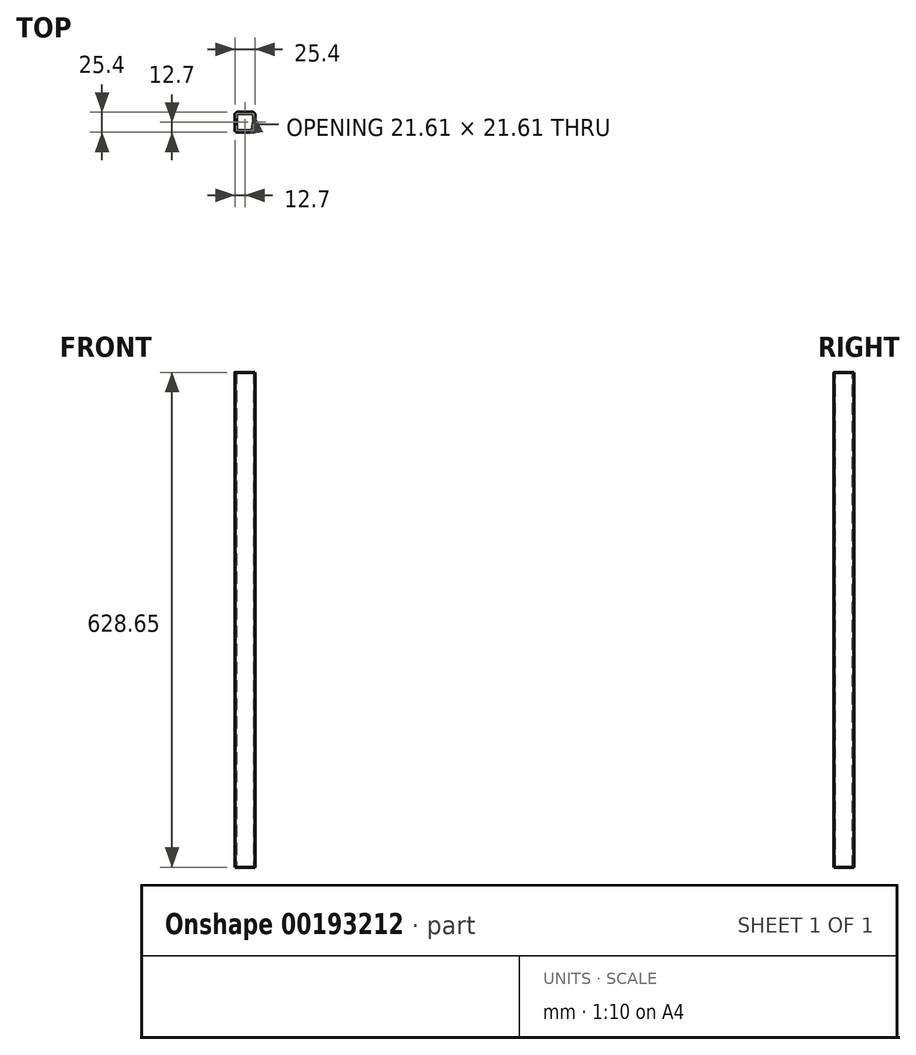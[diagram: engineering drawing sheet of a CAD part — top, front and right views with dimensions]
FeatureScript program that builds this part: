
annotation { "Feature Type Name" : "Feature", "Feature Type Description" : "" }
export const myFeature = defineFeature(function(context is Context, id is Id, definition is map)
    precondition{}
    {
        {
            var Q0;
            Q0=qCreatedBy(makeId("Top.planeOp"),FACE);
            var sketch = newSketch(context, id + "F0", { "sketchPlane" : qUnion([Q0])});
            skLineSegment(sketch, "E0.bottom", {"start": v(3.18, 0) * mm, "end": v(22.23, 0) * mm});
            skLineSegment(sketch, "E0.top", {"start": v(3.18, -25.4) * mm, "end": v(22.23, -25.4) * mm});
            skLineSegment(sketch, "E0.left", {"start": v(0, -3.18) * mm, "end": v(0, -22.23) * mm});
            skLineSegment(sketch, "E0.right", {"start": v(25.4, -3.18) * mm, "end": v(25.4, -22.23) * mm});
            skPoint(sketch, "E1.visualSharp", {"position": v(0, 0) * mm});
            skArc(sketch, "E1.filletArc", {"start": v(3.18, 0) * mm, "mid": v(0.93, -0.93) * mm, "end": v(0, -3.18) * mm});
            skPoint(sketch, "E2.visualSharp", {"position": v(25.4, 0) * mm});
            skArc(sketch, "E2.filletArc", {"start": v(25.4, -3.18) * mm, "mid": v(24.47, -0.93) * mm, "end": v(22.23, 0) * mm});
            skPoint(sketch, "E3.visualSharp", {"position": v(25.4, -25.4) * mm});
            skArc(sketch, "E3.filletArc", {"start": v(22.23, -25.4) * mm, "mid": v(24.47, -24.47) * mm, "end": v(25.4, -22.23) * mm});
            skPoint(sketch, "E4.visualSharp", {"position": v(0, -25.4) * mm});
            skArc(sketch, "E4.filletArc", {"start": v(0, -22.23) * mm, "mid": v(0.93, -24.47) * mm, "end": v(3.18, -25.4) * mm});
            skSolve(sketch);
        }
        {
            var Q0;
            Q0 = qSketchRegion(id + "F0", true);
            extrude(context, id + "F1", {"entities" : qUnion([Q0]), "depth" : 628.65 * mm});
        }
        {
            var Q0;
            Q0=makeQuery(id+"F1.opExtrude","CAP_FACE",FACE,{"disambiguationData":[OSD([sQuery(id+"F0.wireOp",EDGE,"E0.bottom"),sQuery(id+"F0.wireOp",EDGE,"E0.top"),sQuery(id+"F0.wireOp",EDGE,"E0.left"),sQuery(id+"F0.wireOp",EDGE,"E0.right"),sQuery(id+"F0.wireOp",EDGE,"E1.filletArc"),sQuery(id+"F0.wireOp",EDGE,"E2.filletArc"),sQuery(id+"F0.wireOp",EDGE,"E3.filletArc"),sQuery(id+"F0.wireOp",EDGE,"E4.filletArc")])],"isStart":false});
            var Q1;
            Q1=makeQuery(id+"F1.opExtrude","CAP_FACE",FACE,{"disambiguationData":[OSD([sQuery(id+"F0.wireOp",EDGE,"E0.bottom"),sQuery(id+"F0.wireOp",EDGE,"E0.top"),sQuery(id+"F0.wireOp",EDGE,"E0.left"),sQuery(id+"F0.wireOp",EDGE,"E0.right"),sQuery(id+"F0.wireOp",EDGE,"E1.filletArc"),sQuery(id+"F0.wireOp",EDGE,"E2.filletArc"),sQuery(id+"F0.wireOp",EDGE,"E3.filletArc"),sQuery(id+"F0.wireOp",EDGE,"E4.filletArc")])],"isStart":true});
            shell(context, id + "F2", {"entities" : qUnion([Q0, Q1]), "thickness" : 1.9 * mm});
        }
    });
